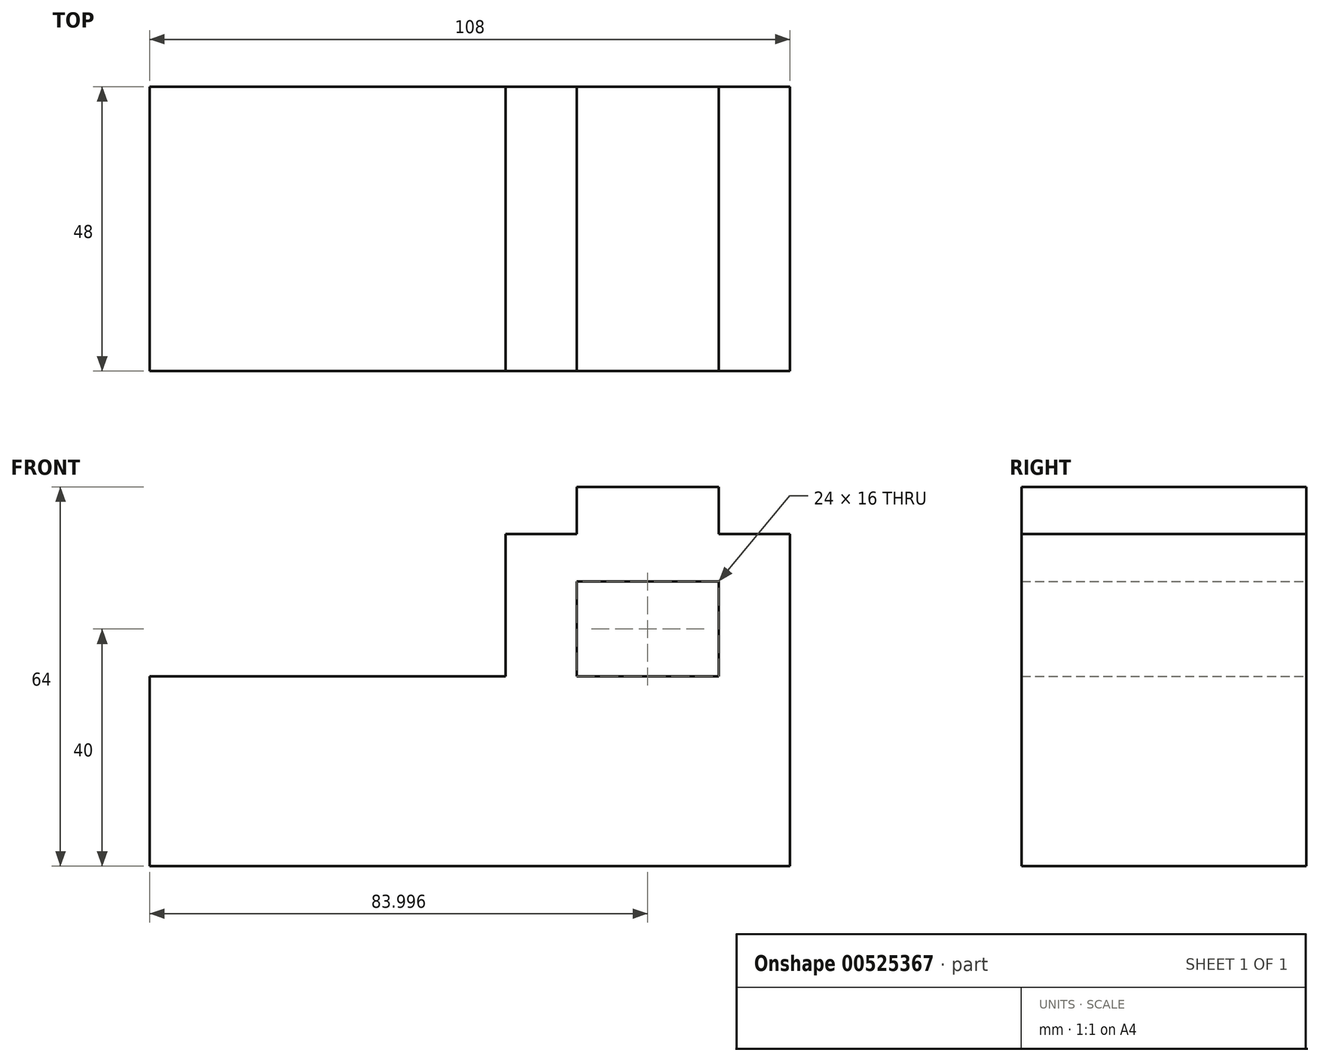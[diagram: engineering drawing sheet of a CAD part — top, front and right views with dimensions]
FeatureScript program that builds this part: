
annotation { "Feature Type Name" : "Feature", "Feature Type Description" : "" }
export const myFeature = defineFeature(function(context is Context, id is Id, definition is map)
    precondition{}
    {
        {
            var Q0;
            Q0=qCreatedBy(makeId("Front.planeOp"),FACE);
            var sketch = newSketch(context, id + "F0", { "sketchPlane" : qUnion([Q0])});
            skLineSegment(sketch, "E0", {"start": v(-40.32, 0) * mm, "end": v(19.68, 0) * mm});
            skLineSegment(sketch, "E1", {"start": v(19.68, 0) * mm, "end": v(19.68, 24) * mm});
            skLineSegment(sketch, "E2", {"start": v(19.68, 24) * mm, "end": v(31.68, 24) * mm});
            skLineSegment(sketch, "E3", {"start": v(31.68, 24) * mm, "end": v(31.68, 32) * mm});
            skLineSegment(sketch, "E4", {"start": v(31.68, 32) * mm, "end": v(55.68, 32) * mm});
            skLineSegment(sketch, "E5", {"start": v(55.68, 32) * mm, "end": v(55.68, 24) * mm});
            skLineSegment(sketch, "E6", {"start": v(55.68, 24) * mm, "end": v(67.68, 24) * mm});
            skLineSegment(sketch, "E7", {"start": v(67.68, 24) * mm, "end": v(67.68, -32) * mm});
            skLineSegment(sketch, "E8", {"start": v(67.68, -32) * mm, "end": v(-40.32, -32) * mm});
            skLineSegment(sketch, "E9", {"start": v(-40.32, -32) * mm, "end": v(-40.32, 0) * mm});
            skLineSegment(sketch, "E10", {"start": v(67.68, 24) * mm, "end": v(67.68, 16) * mm});
            skLineSegment(sketch, "E11", {"start": v(55.68, 16) * mm, "end": v(55.68, 0) * mm});
            skLineSegment(sketch, "E12", {"start": v(55.68, 0) * mm, "end": v(31.68, 0) * mm});
            skLineSegment(sketch, "E13", {"start": v(31.68, 16) * mm, "end": v(55.68, 16) * mm});
            skLineSegment(sketch, "E14", {"start": v(31.68, 16) * mm, "end": v(31.68, 0) * mm});
            skSolve(sketch);
        }
        {
            var Q0;
            Q0=makeQuery(id+"F0.imprint","IMPRINT",FACE,{"disambiguationData":[TD([[makeQuery(id+"F0.imprint","IMPRINT",EDGE,{"derivedFrom":sQuery(id+"F0.wireOp",EDGE,"E0")}),-1.0]])]});
            extrude(context, id + "F1", {"entities" : qUnion([Q0]), "endBound" : BoundingType.SYMMETRIC, "depth" : 48 * mm, "offsetDistance" : 25 * mm});
        }
    });
